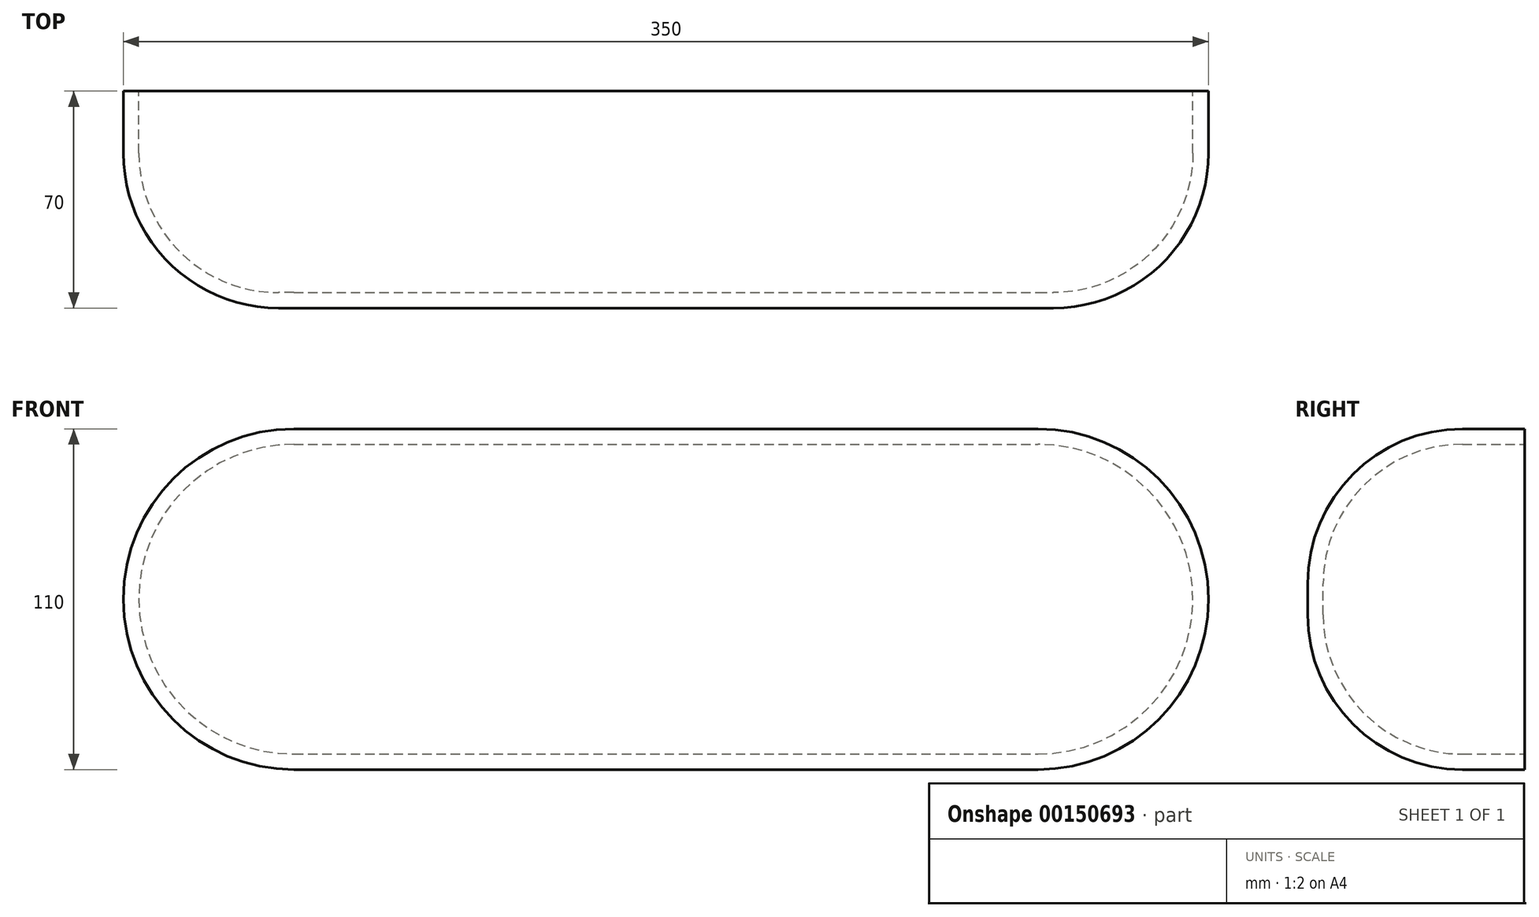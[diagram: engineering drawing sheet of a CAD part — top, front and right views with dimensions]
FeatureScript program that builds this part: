
annotation { "Feature Type Name" : "Feature", "Feature Type Description" : "" }
export const myFeature = defineFeature(function(context is Context, id is Id, definition is map)
    precondition{}
    {
        {
            var Q0;
            Q0=qCreatedBy(makeId("Front.planeOp"),FACE);
            var sketch = newSketch(context, id + "F0", { "sketchPlane" : qUnion([Q0])});
            skLineSegment(sketch, "E0.bottom", {"start": v(-44.39, 127.26) * mm, "end": v(195.61, 127.26) * mm});
            skLineSegment(sketch, "E0.top", {"start": v(-44.39, 17.26) * mm, "end": v(195.61, 17.26) * mm});
            skLineSegment(sketch, "E0.left", {"start": v(-99.39, 72.26) * mm, "end": v(-99.39, 72.26) * mm});
            skLineSegment(sketch, "E0.right", {"start": v(250.61, 72.26) * mm, "end": v(250.61, 72.26) * mm});
            skPoint(sketch, "E1.visualSharp", {"position": v(-99.39, 127.26) * mm});
            skArc(sketch, "E1.filletArc", {"start": v(-44.39, 127.26) * mm, "mid": v(-83.28, 111.15) * mm, "end": v(-99.39, 72.26) * mm});
            skPoint(sketch, "E2.visualSharp", {"position": v(-99.39, 17.26) * mm});
            skArc(sketch, "E2.filletArc", {"start": v(-99.39, 72.26) * mm, "mid": v(-83.28, 33.37) * mm, "end": v(-44.39, 17.26) * mm});
            skPoint(sketch, "E3.visualSharp", {"position": v(250.61, 17.26) * mm});
            skArc(sketch, "E3.filletArc", {"start": v(195.61, 17.26) * mm, "mid": v(234.5, 33.37) * mm, "end": v(250.61, 72.26) * mm});
            skPoint(sketch, "E4.visualSharp", {"position": v(250.61, 127.26) * mm});
            skArc(sketch, "E4.filletArc", {"start": v(250.61, 72.26) * mm, "mid": v(234.5, 111.15) * mm, "end": v(195.61, 127.26) * mm});
            skSolve(sketch);
        }
        {
            var Q0;
            Q0=makeQuery(id+"F0.imprint","IMPRINT",FACE,{"disambiguationData":[TD([[makeQuery(id+"F0.imprint","IMPRINT",EDGE,{"derivedFrom":sQuery(id+"F0.wireOp",EDGE,"E0.bottom")}),-1.0]])]});
            extrude(context, id + "F1", {"entities" : qUnion([Q0]), "depth" : 70 * mm});
        }
        {
            var Q0;
            Q0=makeQuery(id+"F1.opExtrude","CAP_EDGE",EDGE,{"disambiguationData":[OSD([sQuery(id+"F0.wireOp",EDGE,"E0.bottom")])],"isStart":false});
            var Q1;
            Q1=makeQuery(id+"F1.opExtrude","CAP_EDGE",EDGE,{"disambiguationData":[OSD([sQuery(id+"F0.wireOp",EDGE,"E1.filletArc"),sQuery(id+"F0.wireOp",EDGE,"E2.filletArc")])],"isStart":false});
            var Q2;
            Q2=makeQuery(id+"F1.opExtrude","CAP_EDGE",EDGE,{"disambiguationData":[OSD([sQuery(id+"F0.wireOp",EDGE,"E0.top")])],"isStart":false});
            var Q3;
            Q3=makeQuery(id+"F1.opExtrude","CAP_EDGE",EDGE,{"disambiguationData":[OSD([sQuery(id+"F0.wireOp",EDGE,"E3.filletArc"),sQuery(id+"F0.wireOp",EDGE,"E4.filletArc")])],"isStart":false});
            fillet(context, id + "F2", {"entities" : qUnion([Q0, Q1, Q2, Q3]), "radius" : 50 * mm, "tangentPropagation" : true, "allowEdgeOverflow" : false});
        }
        {
            var Q0;
            Q0=makeQuery(id+"F1.opExtrude","CAP_FACE",FACE,{"disambiguationData":[OSD([sQuery(id+"F0.wireOp",EDGE,"E0.bottom"),sQuery(id+"F0.wireOp",EDGE,"E0.top"),sQuery(id+"F0.wireOp",EDGE,"E1.filletArc"),sQuery(id+"F0.wireOp",EDGE,"E2.filletArc"),sQuery(id+"F0.wireOp",EDGE,"E3.filletArc"),sQuery(id+"F0.wireOp",EDGE,"E4.filletArc")])],"isStart":true});
            shell(context, id + "F3", {"entities" : qUnion([Q0]), "thickness" : 5 * mm});
        }
    });
